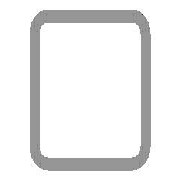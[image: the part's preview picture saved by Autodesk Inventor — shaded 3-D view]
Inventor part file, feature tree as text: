
AUTODESK INVENTOR PART (.ipt)
format: ipt  version: 2019 (Build 230136000, 136)  size: 130,048 bytes
history: native  units: mm (DEFAULTED — no unit token found)
features: other x4, sketch x3, plane x1
ambient origin geometry x8: Origin, YZ Plane, XZ Plane, XY Plane, X Axis, Y Axis, Z Axis, Center Point
bodies: Solid1 (feature_tree), Body (feature_tree)
feature tree (8):
  parser-record x1  (decoder bookkeeping rows leaked as tree rows — omitted from the tree; the rows remain in map.json)
  other  "Driven Length"
  other  "Start plane"
  other  "End plane"
  sketch  "Sketch"  dims[d7=4.0mm d9=20.0mm d11=20.0mm d12=2.0mm d13=-0.0mm d14=1100.0mm d15=10.0mm d16=10.0mm d17=90.0deg d18=1100.0mm]
  sketch  "Sketch3"  dims[d3=1100.0mm]
  plane  "Work Plane3"
  sketch  "Sketch4"  dims[d4=0.0mm]
